# Revit family: HERZ Strömax Commissioning Valve With Test points, Straight Body 4218 GMF
name_source: partatom
category: Rohrzubehör
units: mm (PartAtom-declared; Revit-internal decimal feet)

## family parameters
Arbeitsebenenbasiert = Nein
Beim Laden mit Abzugskörper schneiden = Nein
Bemaßung runder Anschluss = Durchmesser verwenden
Gemeinsam genutzt = Nein
Immer vertikal = Ja
OmniClass-Nummer = 23.65.55.14
OmniClass-Titel = Valves for Liquid Services
Teiletyp = Unterbricht

## types (1)
- HERZ Strömax Commissioning Valve With Test points, Straight Body 4218 GMF
    Body = grey cast iron GJL 250 according to EN 1561
    Differential pressure measurement = The STRÖMAX GMF double regulating and commissioning valve is equipped with two test points:
If a suitable measuring device is used, the differential pressure can be measured and the respective flow rate can be determined depending on the setting level.
The respective flow rate can also be read directly on the HERZ measuring computer (see device manual).
    Field of application = For hydraulic balancing in heating or cooling systems, regulating and shutting off distribution circuits, heat ex-changers, heating and cooling terminals.
    GT = 10 mm  [stored 0.0328084 ft]
    H07 = 10 mm  [stored 0.0328084 ft]
    Hersteller = HERZ Armaturen Ges.m.b.H.
    Max. operating pressure = 1600000.0 Pa
    Max. operating temperature (from DN40) = 110 °C
    Max. operating temperature (up to DN32) = 130 °C
    Medium = Water purity in accordance with the ÖNORM H 5195 and VDI 2035 standards.
Ethylene and propylene glycol can be used in a ratio of 25-50 vol. [%] are mixed.
    Model = The STRÖMAX GMF commissioning valve with measuring valve, straight body DN 25 - 150:
Body of grey cast iron GJL 250 according to EN 1561, flange according to EN 1092, PN 16;
length according to ÖNORM EN-558-1, basic series 1; painted blue.
Thermostatic upper part of brass to DN 100; from DN 125 thermstatic upper part of grey cast iron.
Digital display of the pre-setting levels.
Non-rising spindle with double O-ring seal.
    O-Ring = EPDM
    SCRNCODE = 05;07;02
    SCRNSEQ = ARM;ARM_TYP="STRV";2
    URL = www.herzvalves.com
    Upper part (from DN125) = grey cast iron
    Upper part (up to DN100) = brass
    W02 = 60.00°

note: [stored X ft] marks values corroborated as IEEE doubles in the binary element streams (Revit-internal decimal feet)
